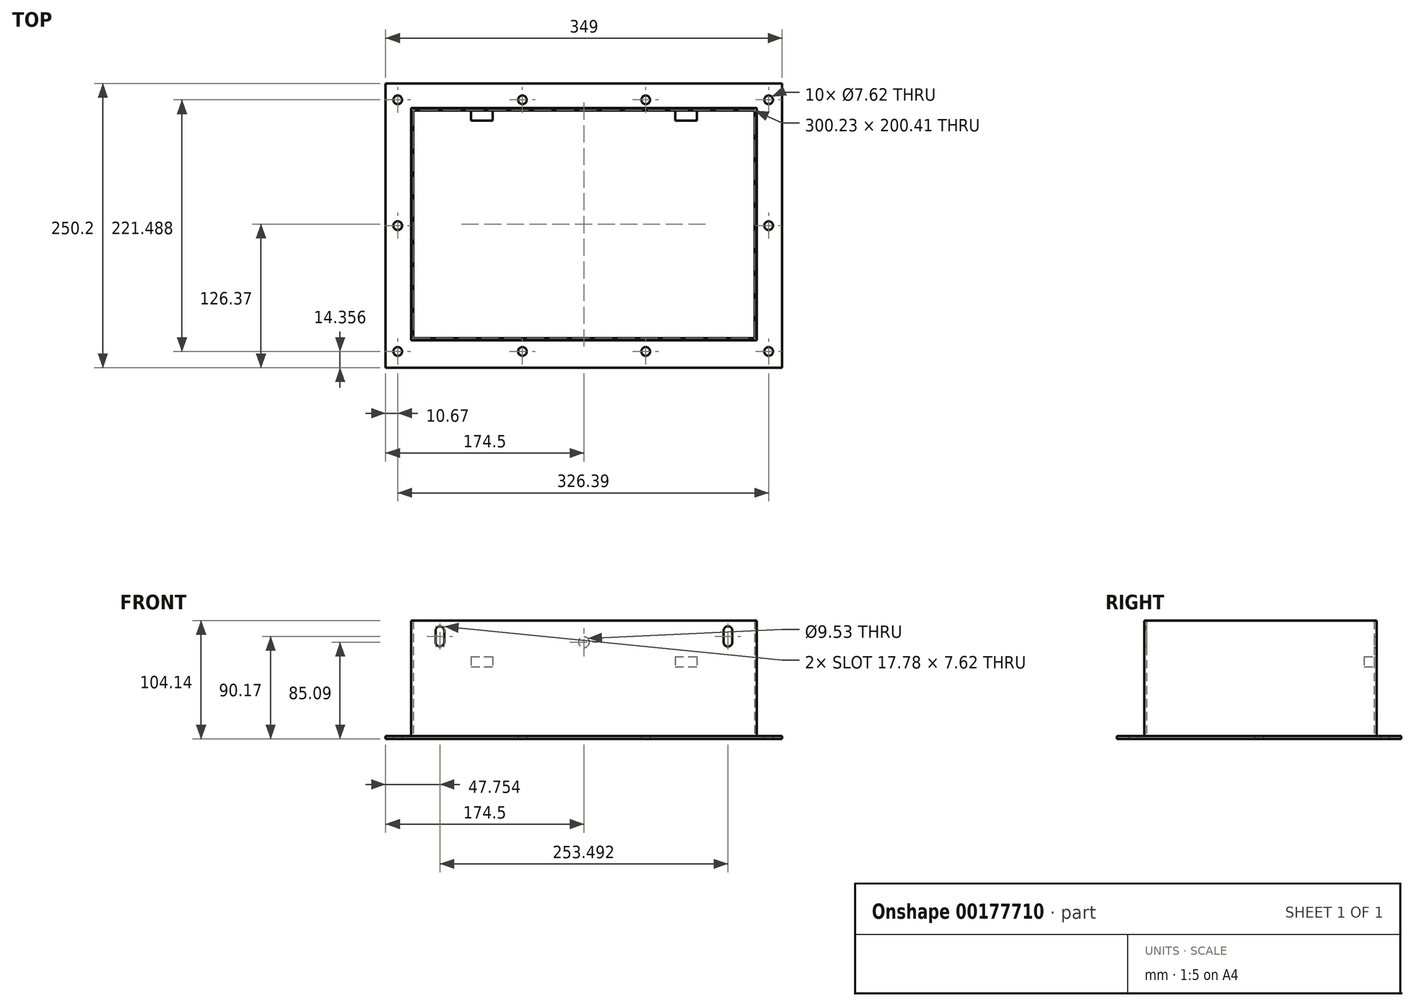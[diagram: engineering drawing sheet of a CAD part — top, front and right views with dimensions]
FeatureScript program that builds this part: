
annotation { "Feature Type Name" : "Feature", "Feature Type Description" : "" }
export const myFeature = defineFeature(function(context is Context, id is Id, definition is map)
    precondition{}
    {
        {
            var Q0;
            Q0=qCreatedBy(makeId("Top.planeOp"),FACE);
            var sketch = newSketch(context, id + "F0", { "sketchPlane" : qUnion([Q0])});
            skLineSegment(sketch, "E0.bottom", {"start": v(174.5, 123.83) * mm, "end": v(-174.5, 123.83) * mm});
            skLineSegment(sketch, "E0.top", {"start": v(174.5, -123.83) * mm, "end": v(-174.5, -123.83) * mm});
            skLineSegment(sketch, "E0.left", {"start": v(174.5, 123.83) * mm, "end": v(174.5, -123.83) * mm});
            skLineSegment(sketch, "E0.right", {"start": v(-174.5, 123.82) * mm, "end": v(-174.5, -123.82) * mm});
            skPoint(sketch, "E0.middle", {"position": v(0, 0) * mm});
            skLineSegment(sketch, "E1", {"start": v(-150.11, 100.2) * mm, "end": v(150.11, 100.2) * mm});
            skLineSegment(sketch, "E2", {"start": v(-150.11, -100.2) * mm, "end": v(150.11, -100.2) * mm});
            skLineSegment(sketch, "E3", {"start": v(-150.11, 100.2) * mm, "end": v(-150.11, -100.2) * mm});
            skLineSegment(sketch, "E4", {"start": v(150.11, 100.2) * mm, "end": v(150.11, -100.2) * mm});
            skCircle(sketch, "E5", {"center": v(162.56, -112.01) * mm, "radius": 3.81 * mm});
            skCircle(sketch, "E6", {"center": v(54.36, -112.01) * mm, "radius": 3.81 * mm});
            skCircle(sketch, "E7", {"center": v(-54.1, -112.01) * mm, "radius": 3.81 * mm});
            skCircle(sketch, "E8", {"center": v(-163.83, -112.01) * mm, "radius": 3.81 * mm});
            skCircle(sketch, "E9", {"center": v(-163.83, -1.27) * mm, "radius": 3.81 * mm});
            skCircle(sketch, "E10", {"center": v(-163.83, 109.47) * mm, "radius": 3.81 * mm});
            skCircle(sketch, "E11", {"center": v(-54.1, 109.47) * mm, "radius": 3.81 * mm});
            skCircle(sketch, "E12", {"center": v(54.36, 109.47) * mm, "radius": 3.81 * mm});
            skCircle(sketch, "E13", {"center": v(162.56, 109.47) * mm, "radius": 3.81 * mm});
            skCircle(sketch, "E14", {"center": v(162.56, -1.27) * mm, "radius": 3.81 * mm});
            skSolve(sketch);
        }
        {
            var Q0;
            Q0=qSketchRegion(id+"F0",true);
            extrude(context, id + "F1", {"entities" : qUnion([Q0]), "depth" : 2.54 * mm});
        }
        {
            var Q0;
            Q0=makeQuery(id+"F1.opExtrude","CAP_FACE",FACE,{"disambiguationData":[OSD([sQuery(id+"F0.wireOp",EDGE,"E0.bottom"),sQuery(id+"F0.wireOp",EDGE,"E0.top"),sQuery(id+"F0.wireOp",EDGE,"E0.left"),sQuery(id+"F0.wireOp",EDGE,"E0.right"),sQuery(id+"F0.wireOp",EDGE,"E1"),sQuery(id+"F0.wireOp",EDGE,"E2"),sQuery(id+"F0.wireOp",EDGE,"E3"),sQuery(id+"F0.wireOp",EDGE,"E4"),sQuery(id+"F0.wireOp",EDGE,"E5"),sQuery(id+"F0.wireOp",EDGE,"E6"),sQuery(id+"F0.wireOp",EDGE,"E7"),sQuery(id+"F0.wireOp",EDGE,"E8"),sQuery(id+"F0.wireOp",EDGE,"E9"),sQuery(id+"F0.wireOp",EDGE,"E10"),sQuery(id+"F0.wireOp",EDGE,"E11"),sQuery(id+"F0.wireOp",EDGE,"E12"),sQuery(id+"F0.wireOp",EDGE,"E13"),sQuery(id+"F0.wireOp",EDGE,"E14")])],"isStart":false});
            var sketch = newSketch(context, id + "F2", { "sketchPlane" : qUnion([Q0])});
            skLineSegment(sketch, "E15.0", {"start": v(-152.15, 102.24) * mm, "end": v(-152.15, -102.23) * mm});
            skLineSegment(sketch, "E15.1", {"start": v(-152.15, 102.24) * mm, "end": v(152.15, 102.24) * mm});
            skLineSegment(sketch, "E15.2", {"start": v(152.15, 102.24) * mm, "end": v(152.15, -102.23) * mm});
            skLineSegment(sketch, "E15.3", {"start": v(-152.15, -102.23) * mm, "end": v(152.15, -102.23) * mm});
            skLineSegment(sketch, "E16.0", {"start": v(-150.11, 100.2) * mm, "end": v(-150.11, -100.2) * mm});
            skLineSegment(sketch, "E16.1", {"start": v(-150.11, 100.2) * mm, "end": v(150.11, 100.2) * mm});
            skLineSegment(sketch, "E16.2", {"start": v(150.11, 100.2) * mm, "end": v(150.11, -100.2) * mm});
            skLineSegment(sketch, "E16.3", {"start": v(-150.11, -100.2) * mm, "end": v(150.11, -100.2) * mm});
            skSolve(sketch);
        }
        {
            var Q0;
            Q0 = qSketchRegion(id + "F2", true);
            extrude(context, id + "F3", {"entities" : qUnion([Q0]), "operationType" : NewBodyOperationType.ADD, "depth" : 101.6 * mm});
        }
        {
            var Q0;
            Q0=makeQuery(id+"F3.opExtrude","SWEPT_FACE",FACE,{"disambiguationData":[OSD([sQuery(id+"F2.wireOp",EDGE,"E15.3")])]});
            var sketch = newSketch(context, id + "F4", { "sketchPlane" : qUnion([Q0])});
            skArc(sketch, "E17", {"start": v(122.94, 85.1) * mm, "mid": v(126.75, 81.28) * mm, "end": v(130.56, 85.1) * mm});
            skLineSegment(sketch, "E18", {"start": v(122.94, 85.1) * mm, "end": v(122.94, 95.25) * mm});
            skLineSegment(sketch, "E19", {"start": v(130.56, 85.1) * mm, "end": v(130.56, 95.25) * mm});
            skArc(sketch, "E20", {"start": v(122.94, 95.25) * mm, "mid": v(126.75, 99.06) * mm, "end": v(130.56, 95.25) * mm});
            skArc(sketch, "E21", {"start": v(-130.56, 85.1) * mm, "mid": v(-126.75, 81.28) * mm, "end": v(-122.94, 85.1) * mm});
            skLineSegment(sketch, "E22", {"start": v(-130.56, 85.1) * mm, "end": v(-130.56, 95.25) * mm});
            skLineSegment(sketch, "E23", {"start": v(-122.94, 85.1) * mm, "end": v(-122.94, 95.25) * mm});
            skArc(sketch, "E24", {"start": v(-130.56, 95.25) * mm, "mid": v(-126.75, 99.06) * mm, "end": v(-122.94, 95.25) * mm});
            skSolve(sketch);
        }
        {
            var Q0;
            Q0 = qSketchRegion(id + "F4", true);
            extrude(context, id + "F5", {"entities" : qUnion([Q0]), "operationType" : NewBodyOperationType.REMOVE, "oppositeDirection" : true, "depth" : 25.4 * mm});
        }
        {
            var Q0;
            Q0=makeQuery(id+"F3.boolean.opBoolean","MERGE",FACE,{"derivedFrom":[makeQuery(id+"F1.opExtrude","SWEPT_FACE",FACE,{"disambiguationData":[OSD([sQuery(id+"F0.wireOp",EDGE,"E1")])]}),makeQuery(id+"F3.opExtrude","SWEPT_FACE",FACE,{"disambiguationData":[OSD([sQuery(id+"F2.wireOp",EDGE,"E16.1")])]})]});
            var sketch = newSketch(context, id + "F6", { "sketchPlane" : qUnion([Q0])});
            skLineSegment(sketch, "E25.bottom", {"start": v(-99.31, 72.4) * mm, "end": v(-80.26, 72.4) * mm});
            skLineSegment(sketch, "E25.top", {"start": v(-99.31, 63.5) * mm, "end": v(-80.26, 63.5) * mm});
            skLineSegment(sketch, "E25.left", {"start": v(-99.31, 72.4) * mm, "end": v(-99.31, 63.5) * mm});
            skLineSegment(sketch, "E25.right", {"start": v(-80.26, 72.4) * mm, "end": v(-80.26, 63.5) * mm});
            skLineSegment(sketch, "E26.bottom", {"start": v(80.26, 72.4) * mm, "end": v(99.31, 72.4) * mm});
            skLineSegment(sketch, "E26.top", {"start": v(80.26, 63.5) * mm, "end": v(99.31, 63.5) * mm});
            skLineSegment(sketch, "E26.left", {"start": v(80.26, 72.4) * mm, "end": v(80.26, 63.5) * mm});
            skLineSegment(sketch, "E26.right", {"start": v(99.31, 72.4) * mm, "end": v(99.31, 63.5) * mm});
            skSolve(sketch);
        }
        {
            var Q0;
            Q0 = qSketchRegion(id + "F6", true);
            extrude(context, id + "F7", {"entities" : qUnion([Q0]), "operationType" : NewBodyOperationType.ADD, "depth" : 8.9 * mm});
        }
        {
            var Q0;
            Q0=makeQuery(id+"F1.opExtrude","SWEPT_FACE",FACE,{"disambiguationData":[OSD([sQuery(id+"F0.wireOp",EDGE,"E0.top")])]});
            extrude(context, id + "F8", {"entities" : qUnion([Q0]), "operationType" : NewBodyOperationType.ADD, "depth" : 2.54 * mm});
        }
        {
            var Q0;
            Q0=makeQuery(id+"F3.opExtrude","SWEPT_FACE",FACE,{"disambiguationData":[OSD([sQuery(id+"F2.wireOp",EDGE,"E15.1")])]});
            var sketch = newSketch(context, id + "F9", { "sketchPlane" : qUnion([Q0])});
            skPoint(sketch, "E27", {"position": v(0, 85.1) * mm});
            skPoint(sketch, "E28.0", {"position": v(-80.26, 72.4) * mm});
            skSolve(sketch);
        }
        {
            var Q0;
            Q0=sQuery(id+"F9.wireOp",VERTEX,"E27");
            var Q1;
            Q1=makeQuery(id+"F1.opExtrude","SWEPT_BODY",BODY,{"disambiguationData":[OSD([sQuery(id+"F0.wireOp",EDGE,"E0.bottom"),sQuery(id+"F0.wireOp",EDGE,"E0.top"),sQuery(id+"F0.wireOp",EDGE,"E0.left"),sQuery(id+"F0.wireOp",EDGE,"E0.right"),sQuery(id+"F0.wireOp",EDGE,"E1"),sQuery(id+"F0.wireOp",EDGE,"E2"),sQuery(id+"F0.wireOp",EDGE,"E3"),sQuery(id+"F0.wireOp",EDGE,"E4"),sQuery(id+"F0.wireOp",EDGE,"E5"),sQuery(id+"F0.wireOp",EDGE,"E6"),sQuery(id+"F0.wireOp",EDGE,"E7"),sQuery(id+"F0.wireOp",EDGE,"E8"),sQuery(id+"F0.wireOp",EDGE,"E9"),sQuery(id+"F0.wireOp",EDGE,"E10"),sQuery(id+"F0.wireOp",EDGE,"E11"),sQuery(id+"F0.wireOp",EDGE,"E12"),sQuery(id+"F0.wireOp",EDGE,"E13"),sQuery(id+"F0.wireOp",EDGE,"E14")])]});
            hole(context, id + "F10", {"style" : HoleStyle.SIMPLE, "endStyle" : HoleEndStyle.BLIND, "holeDiameter" : 9.52 * mm, "holeDepth" : 12.7 * mm, "locations" : qUnion([Q0]), "scope" : qUnion([Q1])});
        }
    });
